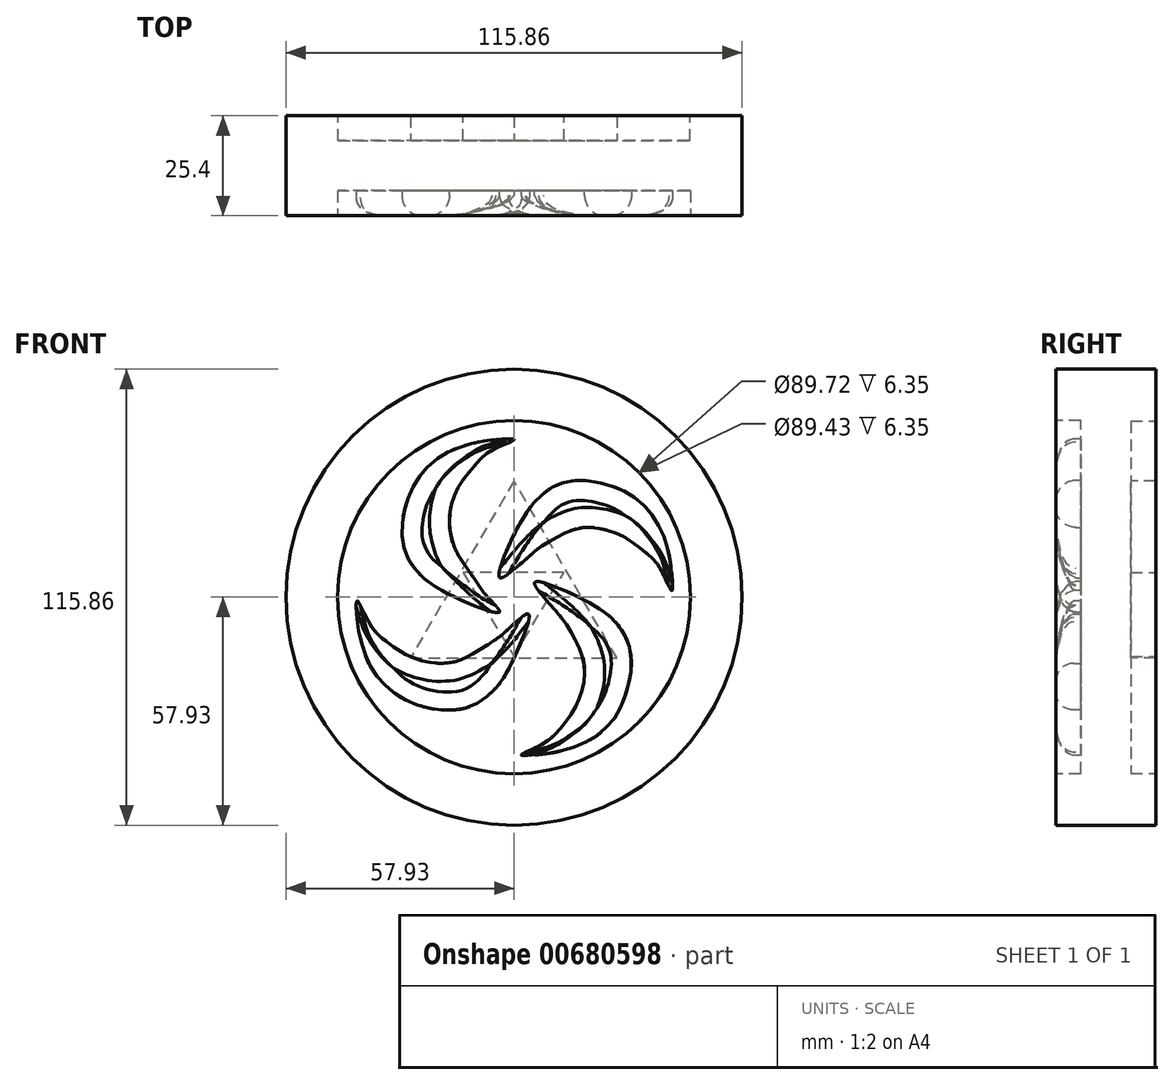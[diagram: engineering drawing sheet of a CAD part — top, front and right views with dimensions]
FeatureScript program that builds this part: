
annotation { "Feature Type Name" : "Feature", "Feature Type Description" : "" }
export const myFeature = defineFeature(function(context is Context, id is Id, definition is map)
    precondition{}
    {
        {
            var Q0;
            Q0=qCreatedBy(makeId("Front.planeOp"),FACE);
            var sketch = newSketch(context, id + "F0", { "sketchPlane" : qUnion([Q0])});
            skCircle(sketch, "E0", {"center": v(0, 0) * mm, "radius": 57.93 * mm});
            skCircle(sketch, "E1", {"center": v(0, 0) * mm, "radius": 45.24 * mm});
            skLineSegment(sketch, "E2", {"start": v(-24.01, 26.9) * mm, "end": v(-4.53, 1.77) * mm});
            skLineSegment(sketch, "E3", {"start": v(-4.53, 1.77) * mm, "end": v(-36.03, 4.88) * mm});
            skLineSegment(sketch, "E4", {"start": v(-36.03, 4.88) * mm, "end": v(-24.01, 26.9) * mm});
            skCircle(sketch, "E5", {"center": v(0, 29.6) * mm, "radius": 10.34 * mm});
            skLineSegment(sketch, "E6", {"start": v(4.46, 1.76) * mm, "end": v(24, 26.88) * mm});
            skLineSegment(sketch, "E7", {"start": v(24, 26.88) * mm, "end": v(36.16, 4.84) * mm});
            skLineSegment(sketch, "E8", {"start": v(36.16, 4.84) * mm, "end": v(4.46, 1.76) * mm});
            skLineSegment(sketch, "E9", {"start": v(0, -5.39) * mm, "end": v(12.64, -34.5) * mm});
            skLineSegment(sketch, "E10", {"start": v(12.64, -34.5) * mm, "end": v(-12.54, -34.5) * mm});
            skLineSegment(sketch, "E11", {"start": v(-12.54, -34.5) * mm, "end": v(0, -5.39) * mm});
            skCircle(sketch, "E12", {"center": v(-26.13, -15.37) * mm, "radius": 10.23 * mm});
            skCircle(sketch, "E13", {"center": v(26.13, -15.19) * mm, "radius": 9.93 * mm});
            skSolve(sketch);
        }
        {
            var Q0;
            Q0=makeQuery(id+"F0.imprint","IMPRINT",FACE,{"disambiguationData":[TD([[makeQuery(id+"F0.imprint","IMPRINT",EDGE,{"derivedFrom":sQuery(id+"F0.wireOp",EDGE,"E0")}),1.0]])]});
            var Q1;
            Q1=makeQuery(id+"F0.imprint","IMPRINT",FACE,{"disambiguationData":[TD([[makeQuery(id+"F0.imprint","IMPRINT",EDGE,{"derivedFrom":sQuery(id+"F0.wireOp",EDGE,"E1")}),1.0]])]});
            var Q2;
            Q2=makeQuery(id+"F0.imprint","IMPRINT",FACE,{"disambiguationData":[TD([[makeQuery(id+"F0.imprint","IMPRINT",EDGE,{"derivedFrom":sQuery(id+"F0.wireOp",EDGE,"E5")}),1.0]])]});
            var Q3;
            Q3=makeQuery(id+"F0.imprint","IMPRINT",FACE,{"disambiguationData":[TD([[makeQuery(id+"F0.imprint","IMPRINT",EDGE,{"derivedFrom":sQuery(id+"F0.wireOp",EDGE,"E2")}),-1.0]])]});
            var Q4;
            Q4=makeQuery(id+"F0.imprint","IMPRINT",FACE,{"disambiguationData":[TD([[makeQuery(id+"F0.imprint","IMPRINT",EDGE,{"derivedFrom":sQuery(id+"F0.wireOp",EDGE,"E12")}),1.0]])]});
            var Q5;
            Q5=makeQuery(id+"F0.imprint","IMPRINT",FACE,{"disambiguationData":[TD([[makeQuery(id+"F0.imprint","IMPRINT",EDGE,{"derivedFrom":sQuery(id+"F0.wireOp",EDGE,"E9")}),-1.0]])]});
            var Q6;
            Q6=makeQuery(id+"F0.imprint","IMPRINT",FACE,{"disambiguationData":[TD([[makeQuery(id+"F0.imprint","IMPRINT",EDGE,{"derivedFrom":sQuery(id+"F0.wireOp",EDGE,"E13")}),1.0]])]});
            var Q7;
            Q7=makeQuery(id+"F0.imprint","IMPRINT",FACE,{"disambiguationData":[TD([[makeQuery(id+"F0.imprint","IMPRINT",EDGE,{"derivedFrom":sQuery(id+"F0.wireOp",EDGE,"E6")}),-1.0]])]});
            extrude(context, id + "F1", {"entities" : qUnion([Q0, Q1, Q2, Q3, Q4, Q5, Q6, Q7]), "depth" : 12.7 * mm, "offsetDistance" : 25.4 * mm});
        }
        {
            var Q0;
            Q0=makeQuery(id+"F1.opExtrude","CAP_FACE",FACE,{"disambiguationData":[OSD([sQuery(id+"F0.wireOp",EDGE,"E0")])],"isStart":true});
            extrude(context, id + "F2", {"entities" : qUnion([Q0]), "operationType" : NewBodyOperationType.ADD, "depth" : 12.7 * mm, "offsetDistance" : 25.4 * mm});
        }
        {
            var Q0;
            Q0=makeQuery(id+"F1.opExtrude","CAP_FACE",FACE,{"disambiguationData":[OSD([sQuery(id+"F0.wireOp",EDGE,"E0")])],"isStart":false});
            var sketch = newSketch(context, id + "F3", { "sketchPlane" : qUnion([Q0])});
            skCircle(sketch, "E14", {"center": v(0, 0) * mm, "radius": 44.86 * mm});
            skSolve(sketch);
        }
        {
            var Q0;
            Q0=makeQuery(id+"F3.imprint","IMPRINT",FACE,{"disambiguationData":[TD([[makeQuery(id+"F3.imprint","IMPRINT",EDGE,{"derivedFrom":sQuery(id+"F3.wireOp",EDGE,"E14")}),1.0]])]});
            extrude(context, id + "F4", {"entities" : qUnion([Q0]), "operationType" : NewBodyOperationType.REMOVE, "oppositeDirection" : true, "depth" : 6.35 * mm, "offsetDistance" : 25.4 * mm});
        }
        {
            var Q0;
            Q0=makeQuery(id+"F2.opExtrude","CAP_FACE",FACE,{"disambiguationData":[OSD([sQuery(id+"F0.wireOp",EDGE,"E0")])],"isStart":false});
            var sketch = newSketch(context, id + "F5", { "sketchPlane" : qUnion([Q0])});
            skCircle(sketch, "E15", {"center": v(0, 0) * mm, "radius": 44.72 * mm});
            skSolve(sketch);
        }
        {
            var Q0;
            Q0=makeQuery(id+"F5.imprint","IMPRINT",FACE,{"disambiguationData":[TD([[makeQuery(id+"F5.imprint","IMPRINT",EDGE,{"derivedFrom":sQuery(id+"F5.wireOp",EDGE,"E15")}),1.0]])]});
            extrude(context, id + "F6", {"entities" : qUnion([Q0]), "operationType" : NewBodyOperationType.REMOVE, "oppositeDirection" : true, "depth" : 6.35 * mm, "offsetDistance" : 25.4 * mm});
        }
        {
            var Q0;
            Q0=makeQuery(id+"F6.boolean.opBoolean","COPY",FACE,{"derivedFrom":makeQuery(id+"F6.opExtrude","CAP_FACE",FACE,{"disambiguationData":[OSD([sQuery(id+"F5.wireOp",EDGE,"E15")])],"isStart":false})});
            var sketch = newSketch(context, id + "F7", { "sketchPlane" : qUnion([Q0])});
            skLineSegment(sketch, "E16", {"start": v(0, 29.52) * mm, "end": v(26.34, -15.44) * mm});
            skLineSegment(sketch, "E17", {"start": v(26.34, -15.44) * mm, "end": v(-26.11, -15.44) * mm});
            skLineSegment(sketch, "E18", {"start": v(-26.11, -15.44) * mm, "end": v(0, 29.52) * mm});
            skLineSegment(sketch, "E19", {"start": v(13.17, 7.04) * mm, "end": v(0.11, -15.44) * mm});
            skLineSegment(sketch, "E20", {"start": v(0.11, -15.44) * mm, "end": v(-13.06, 7.04) * mm});
            skLineSegment(sketch, "E21", {"start": v(-13.06, 7.04) * mm, "end": v(13.17, 7.04) * mm});
            skSolve(sketch);
        }
        {
            var Q0;
            {var subQ3=sQuery(id+"F7.wireOp",EDGE,"E20");Q0=makeQuery(id+"F7.imprint","IMPRINT",FACE,{"disambiguationData":[TD([[makeQuery(id+"F7.imprint","IMPRINT",EDGE,{"derivedFrom":subQ3}),1.0]])]});}
            var Q1;
            Q1=makeQuery(id+"F7.imprint","IMPRINT",FACE,{"disambiguationData":[TD([[makeQuery(id+"F7.imprint","IMPRINT",EDGE,{"derivedFrom":sQuery(id+"F7.wireOp",EDGE,"E19")}),-1.0]])]});
            var Q2;
            {var subQ3=sQuery(id+"F7.wireOp",EDGE,"E21");Q2=makeQuery(id+"F7.imprint","IMPRINT",FACE,{"disambiguationData":[TD([[makeQuery(id+"F7.imprint","IMPRINT",EDGE,{"derivedFrom":subQ3}),1.0]])]});}
            var Q3;
            {var subQ3=sQuery(id+"F7.wireOp",EDGE,"E19");Q3=makeQuery(id+"F7.imprint","IMPRINT",FACE,{"disambiguationData":[TD([[makeQuery(id+"F7.imprint","IMPRINT",EDGE,{"derivedFrom":subQ3}),1.0]])]});}
            extrude(context, id + "F8", {"entities" : qUnion([Q0, Q1, Q2, Q3]), "operationType" : NewBodyOperationType.ADD, "depth" : 6.35 * mm, "offsetDistance" : 25.4 * mm});
        }
        {
            var Q0;
            Q0=makeQuery(id+"F8.opExtrude","CAP_FACE",FACE,{"disambiguationData":[OSD([sQuery(id+"F7.wireOp",EDGE,"E16"),sQuery(id+"F7.wireOp",EDGE,"E17"),sQuery(id+"F7.wireOp",EDGE,"E18")])],"isStart":false});
            var sketch = newSketch(context, id + "F9", { "sketchPlane" : qUnion([Q0])});
            skLineSegment(sketch, "E22", {"start": v(-12.72, 6.35) * mm, "end": v(12.98, 6.35) * mm});
            skLineSegment(sketch, "E23", {"start": v(12.98, 6.35) * mm, "end": v(0, -15) * mm});
            skLineSegment(sketch, "E24", {"start": v(0, -15) * mm, "end": v(-12.72, 6.35) * mm});
            skSolve(sketch);
        }
        {
            var Q0;
            Q0=makeQuery(id+"F9.imprint","IMPRINT",FACE,{"disambiguationData":[TD([[makeQuery(id+"F9.imprint","IMPRINT",EDGE,{"derivedFrom":sQuery(id+"F9.wireOp",EDGE,"E22")}),-1.0]])]});
            extrude(context, id + "F10", {"entities" : qUnion([Q0]), "operationType" : NewBodyOperationType.REMOVE, "oppositeDirection" : true, "depth" : 6.35 * mm, "offsetDistance" : 25.4 * mm});
        }
        {
            var Q0;
            Q0=makeQuery(id+"F4.boolean.opBoolean","COPY",FACE,{"derivedFrom":makeQuery(id+"F4.opExtrude","CAP_FACE",FACE,{"disambiguationData":[OSD([sQuery(id+"F3.wireOp",EDGE,"E14")])],"isStart":false})});
            var sketch = newSketch(context, id + "F11", { "sketchPlane" : qUnion([Q0])});
            skFitSpline(sketch, "E25", {"points": [v(3.66, -4.24) * mm, v(0.46, -14.43) * mm, v(-4.64, -23.07) * mm, v(-9.92, -27.27) * mm, v(-13.93, -28.5) * mm, v(-18.6, -28.59) * mm, v(-23.98, -27.55) * mm, v(-29.4, -25.05) * mm, v(-33.46, -21.6) * mm, v(-36.72, -17.17) * mm, v(-38.8, -11.27) * mm, v(-39.64, -7.4) * mm, v(-39.88, -0.99) * mm, v(-36.72, -6.65) * mm, v(-32.42, -11.27) * mm, v(-27.94, -14.3) * mm, v(-23.41, -16.13) * mm, v(-19.97, -16.75) * mm, v(-15.3, -16.46) * mm, v(-11.29, -14.81) * mm, v(-5.86, -11.56) * mm, v(-1.8, -8.4) * mm, v(3.66, -4.24) * mm]});
            skFitSpline(sketch, "E26", {"points": [v(5.28, 3.76) * mm, v(16.42, 0) * mm, v(24.58, -5.16) * mm, v(27.93, -9.36) * mm, v(29.48, -13.55) * mm, v(29.77, -17.75) * mm, v(28.92, -22.94) * mm, v(27.45, -27.14) * mm, v(25.28, -31) * mm, v(21.7, -34.69) * mm, v(17.88, -37) * mm, v(13.02, -38.8) * mm, v(7.78, -39.83) * mm, v(1.84, -40.07) * mm, v(7.69, -37.1) * mm, v(12.5, -32.42) * mm, v(14.2, -30.3) * mm, v(16.6, -25.63) * mm, v(17.83, -20.91) * mm, v(17.6, -15.96) * mm, v(15.47, -10.68) * mm, v(11.04, -3.98) * mm, v(5.28, 3.76) * mm]});
            skFitSpline(sketch, "E27", {"points": [v(-3.57, 4.95) * mm, v(0, 15.9) * mm, v(4.78, 23.63) * mm, v(8.74, 27.31) * mm, v(13.18, 29.25) * mm, v(18.98, 29.53) * mm, v(24.92, 28.2) * mm, v(28.8, 26.46) * mm, v(32.52, 23.77) * mm, v(35.16, 20.8) * mm, v(37.47, 16.75) * mm, v(39.03, 12.5) * mm, v(39.97, 6.98) * mm, v(40.11, 1.7) * mm, v(37.33, 6.98) * mm, v(34.36, 10.57) * mm, v(30.4, 13.73) * mm, v(26.39, 16.09) * mm, v(22.75, 17.22) * mm, v(18.32, 17.74) * mm, v(13.6, 16.6) * mm, v(9.54, 14.43) * mm, v(5.63, 11.93) * mm, v(-3.57, 4.95) * mm]});
            skFitSpline(sketch, "E28", {"points": [v(-3.73, -3.76) * mm, v(-15.05, 0) * mm, v(-24.15, 6) * mm, v(-27.4, 11) * mm, v(-28.44, 16.71) * mm, v(-27.6, 23.08) * mm, v(-25.43, 28.32) * mm, v(-22.45, 32.57) * mm, v(-18.63, 35.77) * mm, v(-14.72, 37.75) * mm, v(-9.24, 39.36) * mm, v(-4.57, 40.02) * mm, v(0, 40.07) * mm, v(-5.75, 37.24) * mm, v(-9.95, 33.5) * mm, v(-13.54, 28.93) * mm, v(-15.7, 24.17) * mm, v(-16.42, 19.54) * mm, v(-16.04, 15.68) * mm, v(-14.48, 11.24) * mm, v(-12.08, 7.6) * mm, v(-9.34, 3.6) * mm, v(-6.7, 0) * mm, v(-3.73, -3.76) * mm]});
            skSolve(sketch);
        }
        {
            var Q0;
            Q0=makeQuery(id+"F11.imprint","IMPRINT",FACE,{"disambiguationData":[TD([[makeQuery(id+"F11.imprint","IMPRINT",EDGE,{"derivedFrom":sQuery(id+"F11.wireOp",EDGE,"E25")}),-1.0]])]});
            var Q1;
            Q1=makeQuery(id+"F11.imprint","IMPRINT",FACE,{"disambiguationData":[TD([[makeQuery(id+"F11.imprint","IMPRINT",EDGE,{"derivedFrom":sQuery(id+"F11.wireOp",EDGE,"E28")}),-1.0]])]});
            var Q2;
            Q2=makeQuery(id+"F11.imprint","IMPRINT",FACE,{"disambiguationData":[TD([[makeQuery(id+"F11.imprint","IMPRINT",EDGE,{"derivedFrom":sQuery(id+"F11.wireOp",EDGE,"E27")}),-1.0]])]});
            var Q3;
            Q3=makeQuery(id+"F11.imprint","IMPRINT",FACE,{"disambiguationData":[TD([[makeQuery(id+"F11.imprint","IMPRINT",EDGE,{"derivedFrom":sQuery(id+"F11.wireOp",EDGE,"E26")}),-1.0]])]});
            extrude(context, id + "F12", {"entities" : qUnion([Q0, Q1, Q2, Q3]), "operationType" : NewBodyOperationType.ADD, "depth" : 6.35 * mm, "offsetDistance" : 25.4 * mm});
        }
        {
            var Q0;
            Q0=makeQuery(id+"F12.opExtrude","CAP_FACE",FACE,{"disambiguationData":[OSD([sQuery(id+"F11.wireOp",EDGE,"E28")])],"isStart":false});
            fillet(context, id + "F13", {"entities" : qUnion([Q0]), "radius" : 5.08 * mm, "tangentPropagation" : true, "allowEdgeOverflow" : false});
        }
        {
            var Q0;
            Q0=makeQuery(id+"F12.opExtrude","CAP_FACE",FACE,{"disambiguationData":[OSD([sQuery(id+"F11.wireOp",EDGE,"E25")])],"isStart":false});
            fillet(context, id + "F14", {"entities" : qUnion([Q0]), "radius" : 4.57 * mm, "tangentPropagation" : true, "allowEdgeOverflow" : false});
        }
        {
            var Q0;
            Q0=makeQuery(id+"F12.opExtrude","CAP_FACE",FACE,{"disambiguationData":[OSD([sQuery(id+"F11.wireOp",EDGE,"E26")])],"isStart":false});
            fillet(context, id + "F15", {"entities" : qUnion([Q0]), "radius" : 5.08 * mm, "tangentPropagation" : true, "allowEdgeOverflow" : false});
        }
        {
            var Q0;
            Q0=makeQuery(id+"F12.opExtrude","CAP_FACE",FACE,{"disambiguationData":[OSD([sQuery(id+"F11.wireOp",EDGE,"E27")])],"isStart":false});
            fillet(context, id + "F16", {"entities" : qUnion([Q0]), "radius" : 5.08 * mm, "tangentPropagation" : true, "allowEdgeOverflow" : false});
        }
    });
